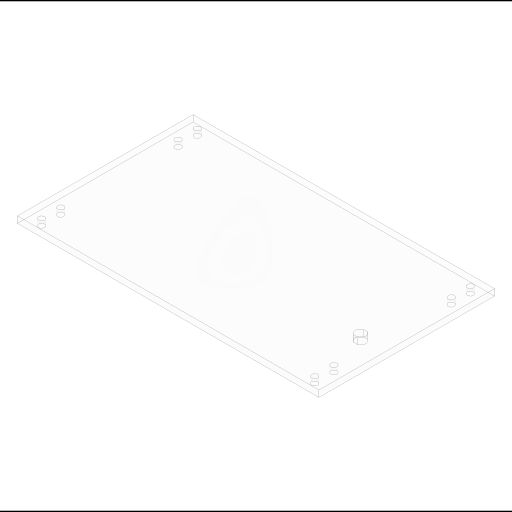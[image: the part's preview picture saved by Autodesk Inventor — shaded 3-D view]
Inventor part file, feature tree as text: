
AUTODESK INVENTOR PART (.ipt)
format: ipt  version: 2023 (Build 270158000, 158)  size: 137,216 bytes
history: native  units: in
note: dims shown in document units (in); Inventor stores cm internally (conversion verified against a paired STEP export)
features: extrude x1
ambient origin geometry x8: Origin, YZ Plane, XZ Plane, XY Plane, X Axis, Y Axis, Z Axis, Center Point
bodies: Body1 (feature_tree)
feature tree (1):
  extrude  "Extrusion2"  Depth=6.1875in
